# Revit family: Light_Fixture-Wall_Sconce-KOHLER-Damask-K-22546_1
name_source: partatom
category: Lighting Fixtures
revit_build: Autodesk Revit 2017 (Build: 20160225_1515(x64)
units: mm (PartAtom-declared; Revit-internal decimal feet)

## family parameters
Cut with Voids When Loaded = No
Host = Face
Light Source = Yes
OmniClass Number = 23.35.47.11
OmniClass Title = Lighting Fixtures
Part Type = Normal
Room Calculation Point = No
Round Connector Dimension = Use Diameter
Shared = No

## types (4) — shared parameters
ADA Compliant = No
Apparent Load = 60 VA
Assembly Code = C1030200
Color Filter = 16777215
Date Modified = 03/24/2020
Default Elevation = 60"
Description = One-light lacemaker sconce
Dimming Lamp Color Temperature Shift = Incandescent Lamp Curve
Electrical Connector = Yes
Electrical Note = One circuit required
Glass Material = Kohler-Glass-L-Crystal_Clear
Height = 11 5/16"
Lamp = Candelabra base (E12) socket, works best with type G or T light bulbs (sold separately)
Length = 10 5/16"
Light Source Symbol Size = 4"
Manufacturer = KOHLER Co.
Master Format 2014 = 26 51 13
Master Format 2014 Name = Interior Lighting Fixtures, Lamps, And Ballasts
Material = Brass Construction
Product Documentation Link = https://www.us.kohler.com
Product Name = Damask
Product Page URL = http://www.us.kohler.com
URL = https://www.us.kohler.com
Voltage = 120 V
WaterSense Certified = No
Wattage Comments = 60 W
Width = 6"

## per-type parameters (varying)
| type | Finish | Model | Type |
| SNL-Polished Nickel | Kohler-Metal-SN-Vibrant_Polished_Nickel | K-22546-SC01-SNL | 1 |
| BGL-Moderne Brushed Gold | Kohler-Metal-BGD-Vibrant_Moderne_Brushed_Gold | K-22546-SC01-BGL | 2 |
| BZL-Oil Rubbed Bronze | Kohler-Metal-2BZ-Oil_Rubbed_Bronze | K-22546-SC01-BZL | 3 |
| CPL-Polished Chrome | Kohler-Metal-CP-Polished_Chrome | K-22546-SC01-CPL | 4 |

## geometry (parser evidence)
native form markers: Sweep x5
no freeform markers — native parametric forms only
